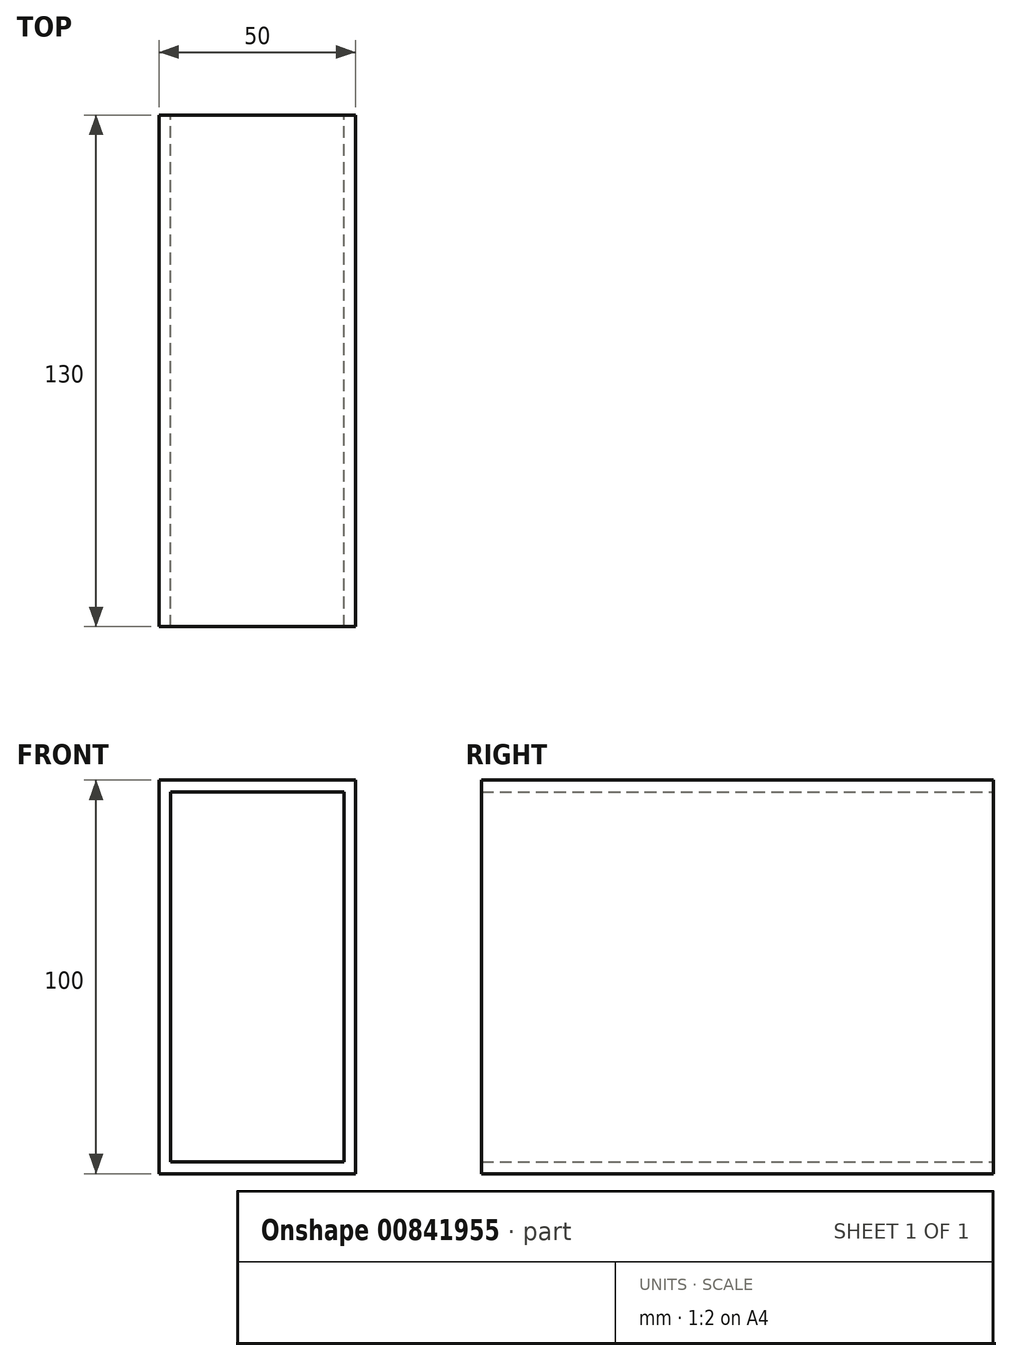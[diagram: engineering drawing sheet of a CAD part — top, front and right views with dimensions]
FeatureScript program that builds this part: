
annotation { "Feature Type Name" : "Feature", "Feature Type Description" : "" }
export const myFeature = defineFeature(function(context is Context, id is Id, definition is map)
    precondition{}
    {
        {
            var Q0;
            Q0=qCreatedBy(makeId("Front.planeOp"),FACE);
            var sketch = newSketch(context, id + "F0", { "sketchPlane" : qUnion([Q0])});
            skLineSegment(sketch, "E0.bottom", {"start": v(-25, 50) * mm, "end": v(25, 50) * mm});
            skLineSegment(sketch, "E0.top", {"start": v(-25, -50) * mm, "end": v(25, -50) * mm});
            skLineSegment(sketch, "E0.left", {"start": v(-25, 50) * mm, "end": v(-25, -50) * mm});
            skLineSegment(sketch, "E0.right", {"start": v(25, 50) * mm, "end": v(25, -50) * mm});
            skLineSegment(sketch, "E1.0", {"start": v(-22, 47) * mm, "end": v(-22, -47) * mm});
            skLineSegment(sketch, "E1.1", {"start": v(-22, 47) * mm, "end": v(22, 47) * mm});
            skLineSegment(sketch, "E1.2", {"start": v(22, 47) * mm, "end": v(22, -47) * mm});
            skLineSegment(sketch, "E1.3", {"start": v(-22, -47) * mm, "end": v(22, -47) * mm});
            skSolve(sketch);
        }
        {
            var Q0;
            Q0=makeQuery(id+"F0.imprint","IMPRINT",FACE,{"disambiguationData":[TD([[makeQuery(id+"F0.imprint","IMPRINT",EDGE,{"derivedFrom":sQuery(id+"F0.wireOp",EDGE,"E0.bottom")}),-1.0]])]});
            extrude(context, id + "F1", {"entities" : qUnion([Q0]), "endBound" : BoundingType.SYMMETRIC, "depth" : 130 * mm, "offsetDistance" : 25 * mm});
        }
    });
